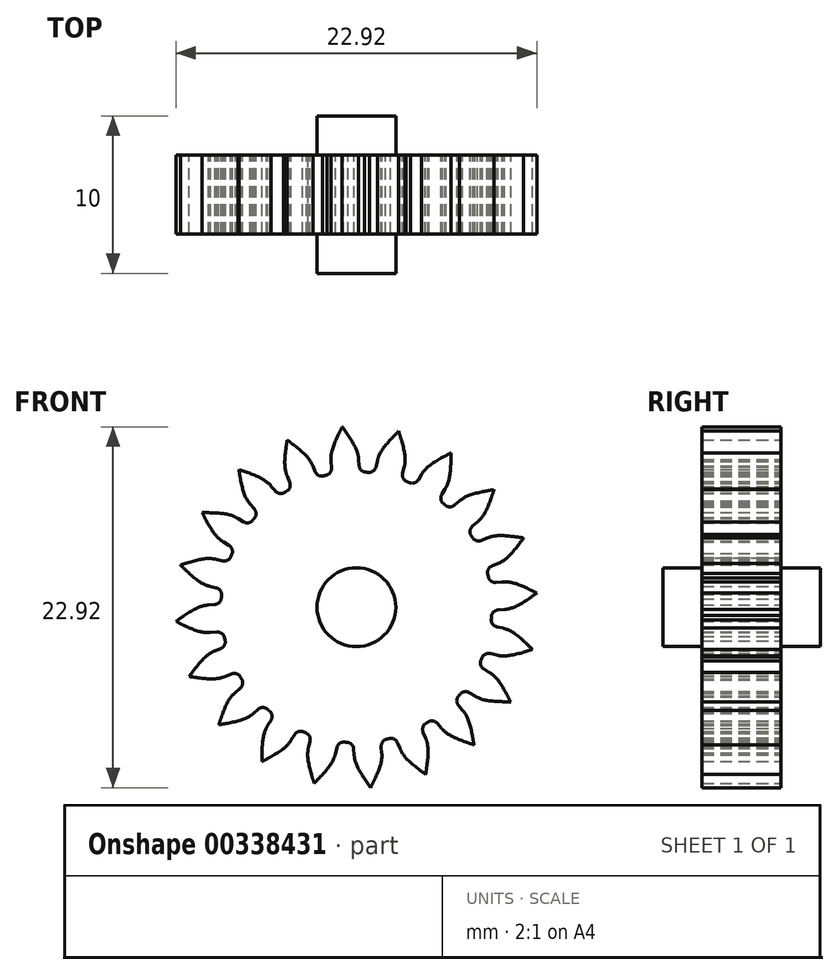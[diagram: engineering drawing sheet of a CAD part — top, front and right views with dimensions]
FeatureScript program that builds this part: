
annotation { "Feature Type Name" : "Feature", "Feature Type Description" : "" }
export const myFeature = defineFeature(function(context is Context, id is Id, definition is map)
    precondition{}
    {
        {
            assignVariable(context, id + "F0", {"name" : "N", "anyValue" : 20});
        }
        {
            assignVariable(context, id + "F1", {"name" : "WoF", "anyValue" : 5});
        }
        {
            var Q0;
            Q0=qCreatedBy(makeId("Front.planeOp"),FACE);
            var sketch = newSketch(context, id + "F2", { "sketchPlane" : qUnion([Q0])});
            skCircle(sketch, "E0", {"center": v(0, 0) * mm, "radius": 8.6 * mm});
            skSolve(sketch);
        }
        {
            var Q0;
            Q0=qSketchRegion(id+"F2",true);
            extrude(context, id + "F3", {"entities" : qUnion([Q0]), "endBound" : BoundingType.SYMMETRIC, "depth" : (getVariable(context, 'WoF')) * mm});
        }
        {
            var Q0;
            Q0=qCreatedBy(makeId("Front.planeOp"),FACE);
            var sketch = newSketch(context, id + "F4", { "sketchPlane" : qUnion([Q0])});
            skCircle(sketch, "E1", {"center": v(0, 0) * mm, "radius": 10 * mm, "construction": true});
            skCircle(sketch, "E2", {"center": v(0, 0) * mm, "radius": 11 * mm, "construction": true});
            skLineSegment(sketch, "E3", {"start": v(0, 0) * mm, "end": v(0, 10) * mm, "construction": true});
            skPoint(sketch, "E4", {"position": v(0, 10) * mm});
            skLineSegment(sketch, "E5", {"start": v(-3.21, 8.83) * mm, "end": v(0, 0) * mm, "construction": true});
            skArc(sketch, "E6", {"start": v(-3.21, 8.83) * mm, "mid": v(-2.06, 9.17) * mm, "end": v(-0.88, 9.36) * mm, "construction": true});
            skArc(sketch, "E7", {"start": v(-3.21, 8.83) * mm, "mid": v(-4.84, 8.06) * mm, "end": v(-6.28, 6.99) * mm, "construction": true});
            skArc(sketch, "E8", {"start": v(-0.88, 9.36) * mm, "mid": v(-0.37, 9.39) * mm, "end": v(0.14, 9.4) * mm, "construction": true});
            skLineSegment(sketch, "E9", {"start": v(0, 10) * mm, "end": v(0, 11) * mm, "construction": true});
            skLineSegment(sketch, "E10", {"start": v(0, 10) * mm, "end": v(-3.21, 8.83) * mm, "construction": true});
            skLineSegment(sketch, "E11", {"start": v(0, 10) * mm, "end": v(-4.58, 10) * mm, "construction": true});
            skLineSegment(sketch, "E12", {"start": v(-6.28, 6.99) * mm, "end": v(-1.06, 11.68) * mm, "construction": true});
            skLineSegment(sketch, "E13", {"start": v(-0.88, 9.36) * mm, "end": v(0.14, 9.45) * mm, "construction": true});
            skLineSegment(sketch, "E14", {"start": v(0, 0) * mm, "end": v(-0.86, 10.97) * mm, "construction": true});
            skCircle(sketch, "E15", {"center": v(0, 0) * mm, "radius": 8.6 * mm, "construction": true});
            skLineSegment(sketch, "E16", {"start": v(0, 0) * mm, "end": v(0.67, 8.57) * mm, "construction": true});
            skPoint(sketch, "E17", {"position": v(0.14, 9.4) * mm});
            skPoint(sketch, "E18", {"position": v(0.14, 9.45) * mm});
            skPoint(sketch, "E19", {"position": v(-1.06, 11.68) * mm});
            skPoint(sketch, "E20", {"position": v(-0.86, 10.97) * mm});
            skPoint(sketch, "E21", {"position": v(0.67, 8.57) * mm});
            skCircle(sketch, "E22", {"center": v(0, 0) * mm, "radius": 9 * mm, "construction": true});
            skFitSpline(sketch, "E23", {"points": [v(-1.06, 11.68) * mm, v(0, 10) * mm, v(0.14, 9.45) * mm, v(0.14, 9.4) * mm], "startDerivative": vector(2.23, -3.09) * mm, "endDerivative": vector(0.01, -0.44) * mm});
            skArc(sketch, "E24", {"start": v(-0.86, 10.97) * mm, "mid": v(-0.72, 10.98) * mm, "end": v(-0.57, 10.99) * mm});
            skLineSegment(sketch, "E25", {"start": v(0.14, 9.4) * mm, "end": v(0.17, 9) * mm});
            skArc(sketch, "E26", {"start": v(0.17, 9) * mm, "mid": v(0.28, 8.73) * mm, "end": v(0.53, 8.58) * mm});
            skArc(sketch, "E27", {"start": v(0.53, 8.58) * mm, "mid": v(-0.07, 8.6) * mm, "end": v(-0.67, 8.57) * mm});
            skArc(sketch, "E28.MirrorCS", {"start": v(-1.86, 8.4) * mm, "mid": v(-1.27, 8.5) * mm, "end": v(-0.67, 8.57) * mm});
            skArc(sketch, "E29.MirrorCS", {"start": v(-1.58, 8.86) * mm, "mid": v(-1.64, 8.58) * mm, "end": v(-1.86, 8.4) * mm});
            skLineSegment(sketch, "E30.MirrorCS", {"start": v(-1.6, 9.26) * mm, "end": v(-1.58, 8.86) * mm});
            skFitSpline(sketch, "E31.MirrorCS", {"points": [v(-0.78, 11.7) * mm, v(-1.56, 9.88) * mm, v(-1.61, 9.31) * mm, v(-1.6, 9.26) * mm], "startDerivative": vector(-1.72, -3.4) * mm, "endDerivative": vector(0.06, -0.43) * mm});
            skArc(sketch, "E32.MirrorCS", {"start": v(-0.86, 10.97) * mm, "mid": v(-1.01, 10.95) * mm, "end": v(-1.16, 10.94) * mm});
            skSolve(sketch);
        }
        {
            var Q0;
            Q0=qSketchRegion(id+"F4",true);
            var Q1;
            Q1=makeQuery(id+"F3.opExtrude","CAP_FACE",FACE,{"disambiguationData":[OSD([sQuery(id+"F2.wireOp",EDGE,"E0"),sQuery(id+"F2.wireOp",EDGE,"ypchOyP9-PMkg-Z84X-TmPn-hLIgu99tQz8k")])],"isStart":false});
            extrude(context, id + "F5", {"entities" : qUnion([Q0]), "endBound" : BoundingType.SYMMETRIC, "endBoundEntityFace" : qUnion([Q1]), "depth" : (getVariable(context, 'WoF')) * mm});
        }
        {
            var Q0;
            Q0=makeQuery(id+"F5.opExtrude","SWEPT_BODY",BODY,{"disambiguationData":[OSD([sQuery(id+"F4.wireOp",EDGE,"E23"),sQuery(id+"F4.wireOp",EDGE,"E24"),sQuery(id+"F4.wireOp",EDGE,"E25"),sQuery(id+"F4.wireOp",EDGE,"E26"),sQuery(id+"F4.wireOp",EDGE,"E27"),sQuery(id+"F4.wireOp",EDGE,"E28.MirrorCS"),sQuery(id+"F4.wireOp",EDGE,"E29.MirrorCS"),sQuery(id+"F4.wireOp",EDGE,"E30.MirrorCS"),sQuery(id+"F4.wireOp",EDGE,"E31.MirrorCS"),sQuery(id+"F4.wireOp",EDGE,"E32.MirrorCS")])]});
            var Q1;
            Q1=makeQuery(id+"F3.opExtrude","CAP_EDGE",EDGE,{"disambiguationData":[OSD([sQuery(id+"F2.wireOp",EDGE,"E0")])],"isStart":false});
            circularPattern(context, id + "F6", {"operationType" : NewBodyOperationType.ADD, "entities" : qUnion([Q0]), "axis" : qUnion([Q1]), "angle" : 360 * degree, "instanceCount" : getVariable(context, 'N'), "equalSpace" : true});
        }
        {
            var Q0;
            Q0=qCreatedBy(makeId("Front.planeOp"),FACE);
            var sketch = newSketch(context, id + "F7", { "sketchPlane" : qUnion([Q0])});
            skCircle(sketch, "E33", {"center": v(0, 0) * mm, "radius": 2.5 * mm});
            skSolve(sketch);
        }
        {
            var Q0;
            Q0 = qSketchRegion(id + "F7", true);
            extrude(context, id + "F8", {"entities" : qUnion([Q0]), "operationType" : NewBodyOperationType.ADD, "endBound" : BoundingType.SYMMETRIC, "depth" : 10 * mm});
        }
    });
